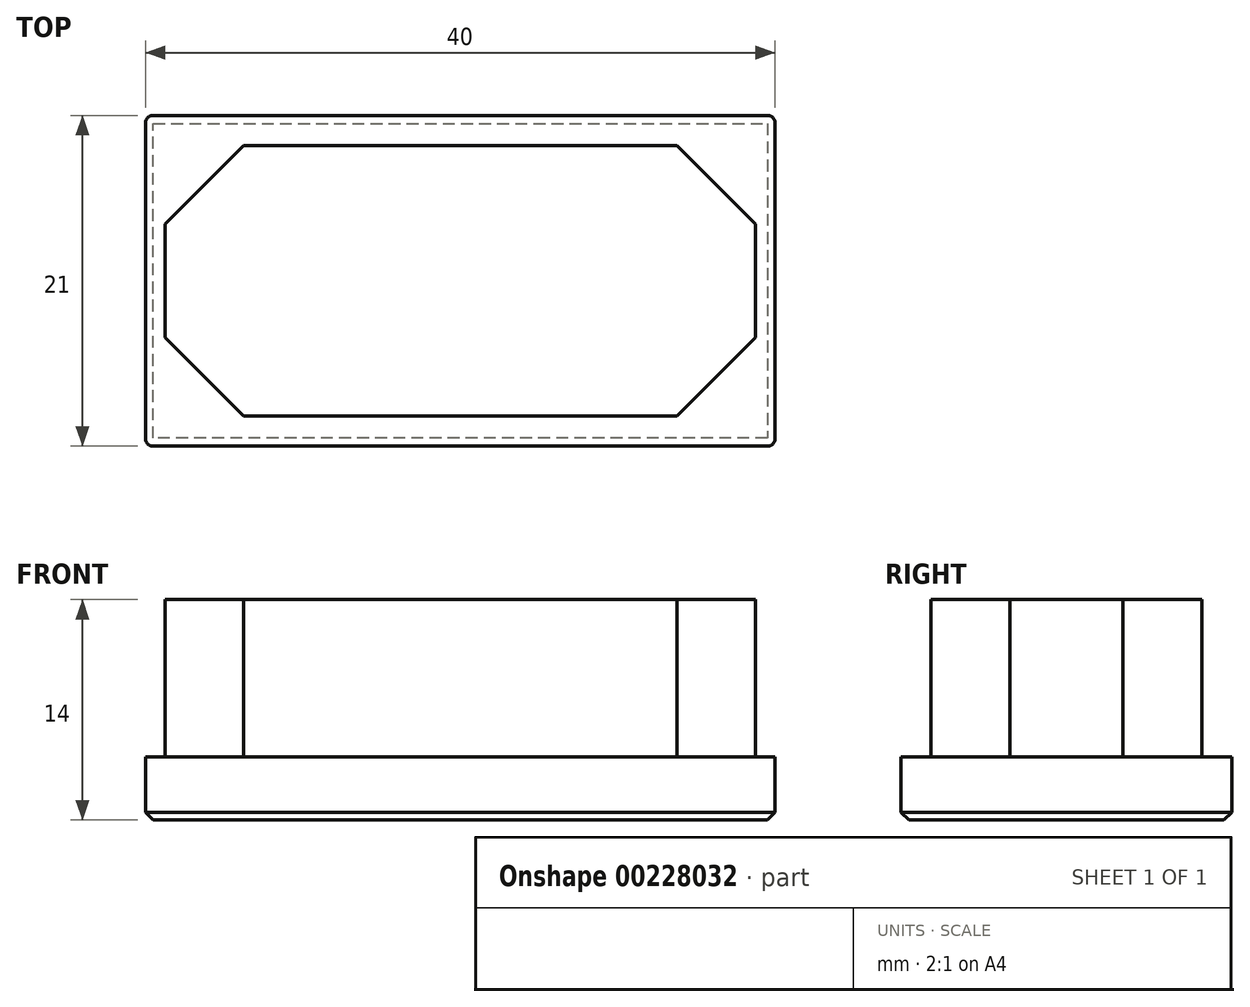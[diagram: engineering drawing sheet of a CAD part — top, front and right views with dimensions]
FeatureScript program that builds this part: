
annotation { "Feature Type Name" : "Feature", "Feature Type Description" : "" }
export const myFeature = defineFeature(function(context is Context, id is Id, definition is map)
    precondition{}
    {
        {
            var Q0;
            Q0=qCreatedBy(makeId("Top.planeOp"),FACE);
            var sketch = newSketch(context, id + "F0", { "sketchPlane" : qUnion([Q0])});
            skLineSegment(sketch, "E0.bottom", {"start": v(20, 10.5) * mm, "end": v(-20, 10.5) * mm});
            skLineSegment(sketch, "E0.top", {"start": v(20, -10.5) * mm, "end": v(-20, -10.5) * mm});
            skLineSegment(sketch, "E0.left", {"start": v(20, 10.5) * mm, "end": v(20, -10.5) * mm});
            skLineSegment(sketch, "E0.right", {"start": v(-20, 10.5) * mm, "end": v(-20, -10.5) * mm});
            skPoint(sketch, "E0.middle", {"position": v(0, 0) * mm});
            skSolve(sketch);
        }
        {
            var Q0;
            Q0 = qSketchRegion(id + "F0", true);
            extrude(context, id + "F1", {"entities" : qUnion([Q0]), "depth" : 4 * mm});
        }
        {
            var Q0;
            Q0=makeQuery(id+"F1.opExtrude","CAP_FACE",FACE,{"disambiguationData":[OSD([sQuery(id+"F0.wireOp",EDGE,"E0.bottom"),sQuery(id+"F0.wireOp",EDGE,"E0.top"),sQuery(id+"F0.wireOp",EDGE,"E0.left"),sQuery(id+"F0.wireOp",EDGE,"E0.right")])],"isStart":false});
            var sketch = newSketch(context, id + "F2", { "sketchPlane" : qUnion([Q0])});
            skLineSegment(sketch, "E1.bottom", {"start": v(18.75, 8.6) * mm, "end": v(-18.75, 8.6) * mm});
            skLineSegment(sketch, "E1.top", {"start": v(18.75, -8.6) * mm, "end": v(-18.75, -8.6) * mm});
            skLineSegment(sketch, "E1.left", {"start": v(18.75, 8.6) * mm, "end": v(18.75, -8.6) * mm});
            skLineSegment(sketch, "E1.right", {"start": v(-18.75, 8.6) * mm, "end": v(-18.75, -8.6) * mm});
            skPoint(sketch, "E1.middle", {"position": v(0, 0) * mm});
            skSolve(sketch);
        }
        {
            var Q0;
            Q0 = qSketchRegion(id + "F2", true);
            extrude(context, id + "F3", {"entities" : qUnion([Q0]), "operationType" : NewBodyOperationType.ADD, "depth" : 10 * mm});
        }
        {
            var Q0;
            Q0=makeQuery(id+"F3.opExtrude","SWEPT_EDGE",EDGE,{"disambiguationData":[OSD([sQuery(id+"F2.wireOp",EDGE,"E1.top"),sQuery(id+"F2.wireOp",EDGE,"E1.left")])]});
            var Q1;
            Q1=makeQuery(id+"F3.opExtrude","SWEPT_EDGE",EDGE,{"disambiguationData":[OSD([sQuery(id+"F2.wireOp",EDGE,"E1.top"),sQuery(id+"F2.wireOp",EDGE,"E1.right")])]});
            var Q2;
            Q2=makeQuery(id+"F3.opExtrude","SWEPT_EDGE",EDGE,{"disambiguationData":[OSD([sQuery(id+"F2.wireOp",EDGE,"E1.bottom"),sQuery(id+"F2.wireOp",EDGE,"E1.left")])]});
            var Q3;
            Q3=makeQuery(id+"F3.opExtrude","SWEPT_EDGE",EDGE,{"disambiguationData":[OSD([sQuery(id+"F2.wireOp",EDGE,"E1.bottom"),sQuery(id+"F2.wireOp",EDGE,"E1.right")])]});
            chamfer(context, id + "F4", {"entities" : qUnion([Q0, Q1, Q2, Q3]), "width" : 5 * mm, "tangentPropagation" : true});
        }
        {
            var Q0;
            Q0=makeQuery(id+"F1.opExtrude","SWEPT_EDGE",EDGE,{"disambiguationData":[OSD([sQuery(id+"F0.wireOp",EDGE,"E0.top"),sQuery(id+"F0.wireOp",EDGE,"E0.right")])]});
            var Q1;
            Q1=makeQuery(id+"F1.opExtrude","SWEPT_EDGE",EDGE,{"disambiguationData":[OSD([sQuery(id+"F0.wireOp",EDGE,"E0.bottom"),sQuery(id+"F0.wireOp",EDGE,"E0.right")])]});
            var Q2;
            Q2=makeQuery(id+"F1.opExtrude","SWEPT_EDGE",EDGE,{"disambiguationData":[OSD([sQuery(id+"F0.wireOp",EDGE,"E0.top"),sQuery(id+"F0.wireOp",EDGE,"E0.left")])]});
            var Q3;
            Q3=makeQuery(id+"F1.opExtrude","SWEPT_EDGE",EDGE,{"disambiguationData":[OSD([sQuery(id+"F0.wireOp",EDGE,"E0.bottom"),sQuery(id+"F0.wireOp",EDGE,"E0.left")])]});
            fillet(context, id + "F5", {"entities" : qUnion([Q0, Q1, Q2, Q3]), "radius" : 0.5 * mm, "tangentPropagation" : true, "allowEdgeOverflow" : false});
        }
        {
            var Q0;
            Q0=makeQuery(id+"F1.opExtrude","CAP_EDGE",EDGE,{"disambiguationData":[OSD([sQuery(id+"F0.wireOp",EDGE,"E0.left")])],"isStart":true});
            chamfer(context, id + "F6", {"entities" : qUnion([Q0]), "width" : 0.5 * mm, "tangentPropagation" : true});
        }
    });
